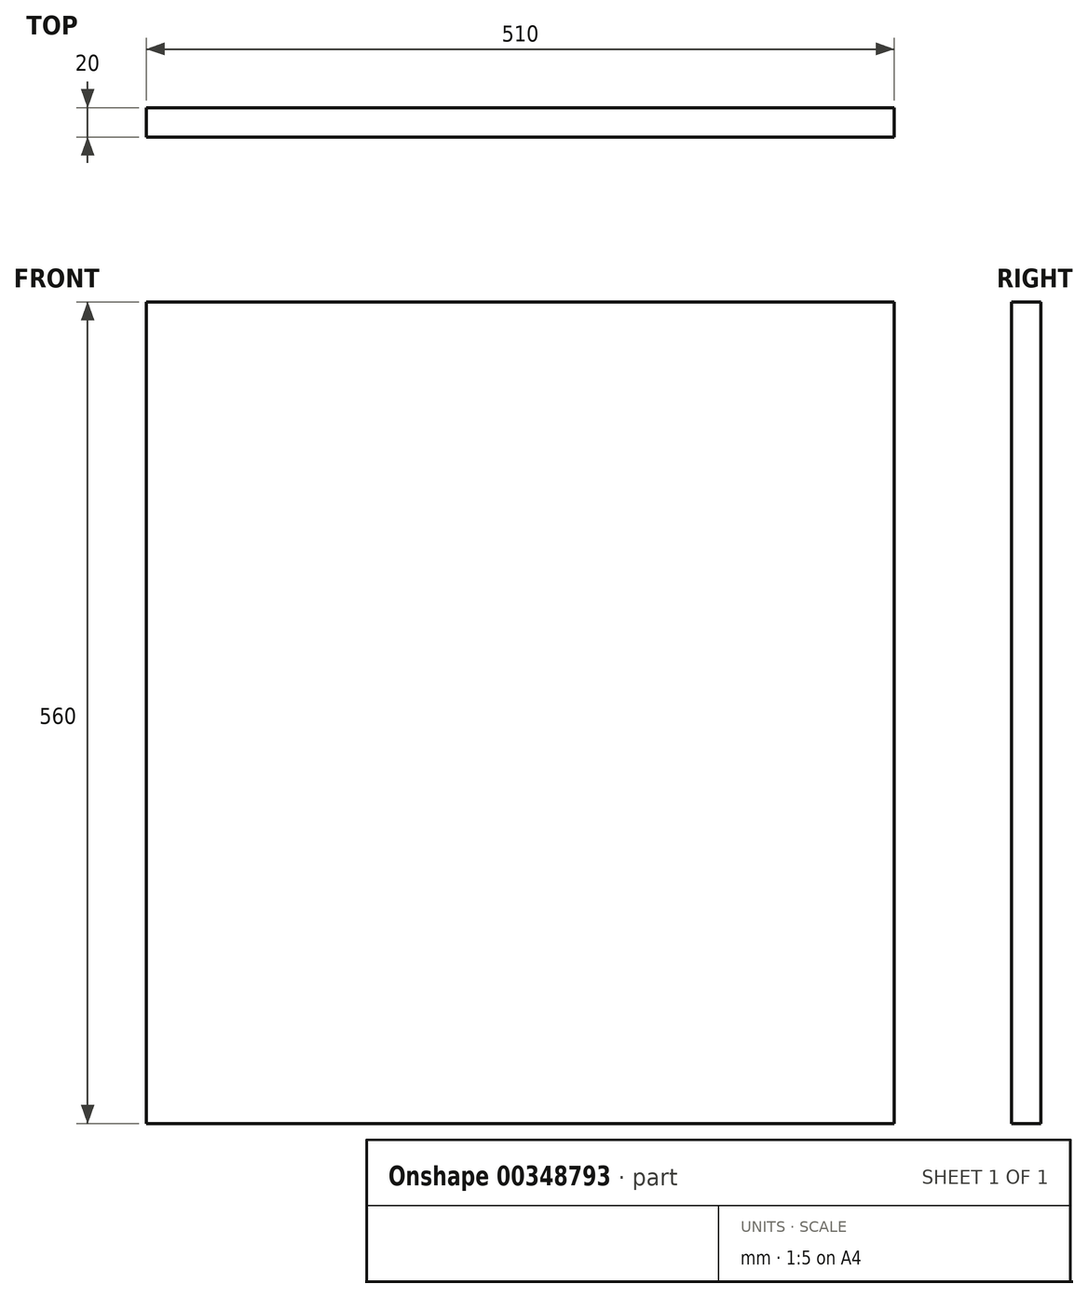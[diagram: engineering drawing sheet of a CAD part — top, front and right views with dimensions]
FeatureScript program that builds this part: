
annotation { "Feature Type Name" : "Feature", "Feature Type Description" : "" }
export const myFeature = defineFeature(function(context is Context, id is Id, definition is map)
    precondition{}
    {
        {
            var Q0;
            Q0=qCreatedBy(makeId("Front.planeOp"),FACE);
            var sketch = newSketch(context, id + "F0", { "sketchPlane" : qUnion([Q0])});
            skLineSegment(sketch, "E0.bottom", {"start": v(-510, -560) * mm, "end": v(0, -560) * mm});
            skLineSegment(sketch, "E0.top", {"start": v(-510, 0) * mm, "end": v(0, 0) * mm});
            skLineSegment(sketch, "E0.left", {"start": v(-510, -560) * mm, "end": v(-510, 0) * mm});
            skLineSegment(sketch, "E0.right", {"start": v(0, -560) * mm, "end": v(0, 0) * mm});
            skSolve(sketch);
        }
        {
            var Q0;
            Q0=qSketchRegion(id+"F0",true);
            extrude(context, id + "F1", {"entities" : qUnion([Q0]), "depth" : 20 * mm});
        }
    });
